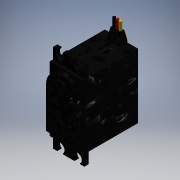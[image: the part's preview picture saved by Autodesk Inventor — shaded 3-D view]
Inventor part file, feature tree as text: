
AUTODESK INVENTOR PART (.ipt)
format: ipt  version: 2019 (Build 230136000, 136)  size: 236,032 bytes
history: native  units: in
note: dims shown in document units (in); Inventor stores cm internally (conversion verified against a paired STEP export)
features: extrude x9, sketch x9, other x4, fillet x2, plane x1, mirror x1, projected_geometry x1, hole x1
ambient origin geometry x8: Origin, YZ Plane, XZ Plane, XY Plane, X Axis, Y Axis, Z Axis, Center Point
bodies: Body1 (feature_tree), Body2 (feature_tree), Body3 (feature_tree)
feature tree (28):
  other  "Servo"
  other  "Blocks"
  extrude  "Extrusion1"  Depth=1.525in
  extrude  "Extrusion2"  Depth=0.025in
  extrude  "Extrusion3"  Depth=0.17in
  fillet  "Fillet1"  Radius=0.11in
  plane  "Work Plane1"
  extrude  "Extrusion4"  Depth=0.07in
  fillet  "Fillet2"  Radius=0.07in
  mirror  "Mirror1"
  extrude  "Extrusion5"  [1 undecoded]
  extrude  "Extrusion6"  Depth=0.28in
  extrude  "Extrusion7"  Depth=0.1in
  extrude  "Extrusion8"  Depth=0.1in TaperAngle=0.0deg
  extrude  "Extrusion9"  Depth=0.3in
  sketch  "Sketch1"  dims[d0=0.782in d1=1.525in]
  sketch  "Sketch2"  dims[d2=1.305in d3=0.0in d4=0.025in]
  sketch  "Sketch3"  dims[d5=0.025in d6=0.17in d7=0.11in d8=0.0in]
  sketch  "Sketch4"  dims[d9=0.508in d11=0.391in d12=0.07in d13=0.0in]
  sketch  "Sketch5"  dims[d14=0.366in d15=-0.16in]
  sketch  "Sketch6"  dims[d16=0.737in d18=0.28in]
  sketch  "Sketch7"  dims[d19=0.1in d20=0.21in d21=0.165in]
  other  "Red wire"
  sketch  "Sketch8"  dims[d22=0.165in d23=0.1in d24=0.0in]
  sketch  "Sketch9"  dims[d25=0.01in d26=0.3in d27=0.17in d28=0.01in d29=0.0625in d30=0.0in d31=0.2in d32=-0.0687in d33=0.0625in d34=0.2in d35=0.0in d36=0.0625in d37=0.04in d38=0.2in d39=0.0in d40=0.0625in d41=0.04in d42=0.2in d43=0.0in d140=0.6299in d141=0.1457in d142=0.6299in d143=0.6299in d144=0.315in]
  other  "Yellow Wire"
  projected_geometry  "Project Cut Edges1"
  hole  "Hole Pattern 4"  [1 undecoded]
note: 2 required parameter values undecoded (feature->parameter linkage not recoverable at this tier; creation-order binding heuristic only, values carry confidence <= 0.55)
